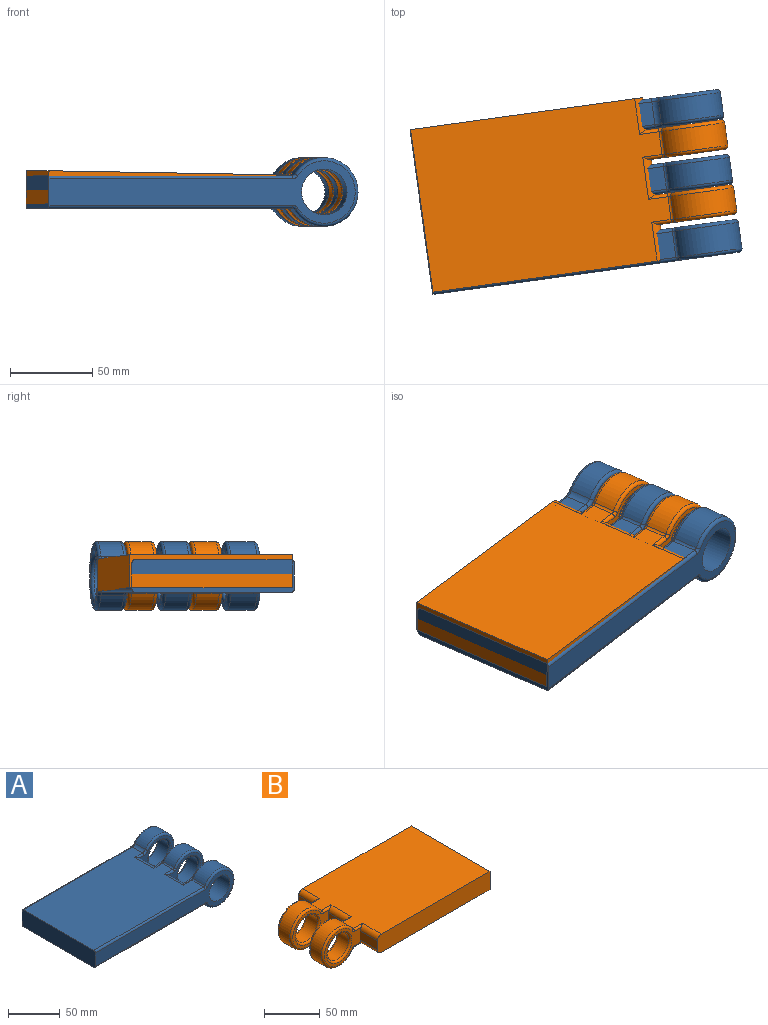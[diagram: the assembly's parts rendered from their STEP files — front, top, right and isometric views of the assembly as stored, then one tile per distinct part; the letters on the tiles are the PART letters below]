
ASSEMBLY  parts=2 mates=1
PART A: 62 faces, bbox 192.2x100x45.5 mm
  f0: plane 149.84x96mm, normal (0,0,-1), area 13745.8mm2, adj f6,f17,f19,f21,f25,f26,f27,f36
  f1: cylinder r=21mm len=42mm, axis (0,-1,0), area 1524.5mm2, adj f24,f26,f29,f34
  f2: cylinder r=21mm len=42mm, axis (0,-1,0), area 1742.3mm2, adj f23,f25,f39,f44
  f3: cylinder r=14mm len=28mm, axis (0,1,0), area 1583.4mm2, adj f8,f60
  f4: cylinder r=21mm len=42mm, axis (0,-1,0), area 1485.7mm2, adj f21,f22,f49,f54
  f5: plane 149.84x96mm, normal (0,0,1), area 13745.8mm2, adj f6,f18,f20,f22,f23,f24,f31,f32
  f6: plane 100x20mm, normal (-1,0,0), area 1996.6mm2, adj f0,f5,f7,f8,f37,f41,f47,f51
  f7: plane 188.46x38mm, normal (0,1,0), area 2751.1mm2, adj f6,f47,f48,f49,f50,f51,f61
  f8: plane 188.46x38mm, normal (0,-1,0), area 2936.7mm2, adj f3,f6,f37,f38,f39,f40,f41
  f9: cylinder r=14mm len=28mm, axis (0,1,0), area 1231.5mm2, adj f58,f61
  f10: plane 46.47x38mm, normal (0,1,0), area 462.3mm2, adj f14,f19,f20,f42,f43,f44,f45,f46
  f11: plane 46.47x38mm, normal (0,1,0), area 462.3mm2, adj f13,f17,f18,f27,f28,f29,f30,f31
  f12: cylinder r=14mm len=28mm, axis (0,1,0), area 1231.5mm2, adj f57,f59
  f13: plane 22x10mm, normal (1,0,0), area 220mm2, adj f11,f16,f17,f18
  f14: plane 22x10mm, normal (1,0,0), area 220mm2, adj f10,f15,f19,f20
  f15: plane 46.47x38mm, normal (0,-1,0), area 462.3mm2, adj f14,f19,f20,f32,f33,f34,f35,f36
  f16: plane 46.47x38mm, normal (0,-1,0), area 465.2mm2, adj f13,f17,f18,f52,f53,f54,f55,f56
  f17: cylinder r=5mm len=26mm, axis (0,1,0), area 179.9mm2, adj f0,f11,f13,f16,f27,f56
  f18: cylinder r=5mm len=26mm, axis (0,1,0), area 179.9mm2, adj f5,f11,f13,f16,f31,f52
  f19: cylinder r=5mm len=26mm, axis (0,1,0), area 179.9mm2, adj f0,f10,f14,f15,f36,f42
  f20: cylinder r=5mm len=26mm, axis (0,1,0), area 179.9mm2, adj f5,f10,f14,f15,f32,f46
  f21: cylinder r=5mm len=14mm, axis (0,-1,0), area 66.9mm2, adj f0,f4,f50,f55
  f22: cylinder r=5mm len=14mm, axis (0,-1,0), area 66.9mm2, adj f4,f5,f48,f53
  f23: cylinder r=2mm len=16mm, axis (0,-1,0), area 32.7mm2, adj f2,f5,f38,f45
  f24: cylinder r=2mm len=14mm, axis (0,-1,0), area 28.6mm2, adj f1,f5,f30,f33
  f25: cylinder r=2mm len=16mm, axis (0,-1,0), area 32.7mm2, adj f0,f2,f40,f43
  f26: cylinder r=2mm len=14mm, axis (0,-1,0), area 28.6mm2, adj f0,f1,f28,f35
  f27: cylinder r=2mm len=11.84mm, axis (-1,0,0), area 30.2mm2, adj f0,f11,f17,f28
  f28: torus R=4mm, axis (0,-1,0), area 8.8mm2, adj f11,f26,f27,f29
  f29: torus R=19mm, axis (0,-1,0), area 330.3mm2, adj f1,f11,f28,f30
  f30: torus R=4mm, axis (0,-1,0), area 8.8mm2, adj f11,f24,f29,f31
  f31: cylinder r=2mm len=11.84mm, axis (1,0,0), area 30.2mm2, adj f5,f11,f18,f30
  f32: cylinder r=2mm len=11.84mm, axis (1,0,0), area 30.2mm2, adj f5,f15,f20,f33
  f33: torus R=4mm, axis (0,1,0), area 8.8mm2, adj f15,f24,f32,f34
  f34: torus R=19mm, axis (0,1,0), area 330.3mm2, adj f1,f15,f33,f35
  f35: torus R=4mm, axis (0,1,0), area 8.8mm2, adj f15,f26,f34,f36
  f36: cylinder r=2mm len=11.84mm, axis (-1,0,0), area 30.2mm2, adj f0,f15,f19,f35
  f37: cylinder r=2mm len=149.84mm, axis (-1,0,0), area 470.7mm2, adj f5,f6,f8,f38
  f38: torus R=4mm, axis (0,-1,0), area 8.8mm2, adj f8,f23,f37,f39
  f39: torus R=19mm, axis (0,-1,0), area 330.3mm2, adj f2,f8,f38,f40
  f40: torus R=4mm, axis (0,-1,0), area 8.8mm2, adj f8,f25,f39,f41
  f41: cylinder r=2mm len=149.84mm, axis (1,0,0), area 470.7mm2, adj f0,f6,f8,f40
  f42: cylinder r=2mm len=11.84mm, axis (-1,0,0), area 30.2mm2, adj f0,f10,f19,f43
  f43: torus R=4mm, axis (0,-1,0), area 8.8mm2, adj f10,f25,f42,f44
  f44: torus R=19mm, axis (0,-1,0), area 330.3mm2, adj f2,f10,f43,f45
  f45: torus R=4mm, axis (0,-1,0), area 8.8mm2, adj f10,f23,f44,f46
  f46: cylinder r=2mm len=11.84mm, axis (1,0,0), area 30.2mm2, adj f5,f10,f20,f45
  f47: cylinder r=2mm len=148.22mm, axis (1,0,0), area 465.7mm2, adj f5,f6,f7,f48
  f48: torus R=7mm, axis (0,-1,0), area 17.2mm2, adj f7,f22,f47,f49
  f49: torus R=19mm, axis (0,-1,0), area 321.8mm2, adj f4,f7,f48,f50
  f50: torus R=7mm, axis (0,-1,0), area 17.2mm2, adj f7,f21,f49,f51
  f51: cylinder r=2mm len=148.22mm, axis (-1,0,0), area 465.7mm2, adj f0,f6,f7,f50
  f52: cylinder r=2mm len=10.23mm, axis (1,0,0), area 25.1mm2, adj f5,f16,f18,f53
  f53: torus R=7mm, axis (0,1,0), area 17.2mm2, adj f16,f22,f52,f54
  f54: torus R=19mm, axis (0,1,0), area 321.8mm2, adj f4,f16,f53,f55
  f55: torus R=7mm, axis (0,1,0), area 17.2mm2, adj f16,f21,f54,f56
  f56: cylinder r=2mm len=10.23mm, axis (-1,0,0), area 25.1mm2, adj f0,f16,f17,f55
  f57: torus R=16mm, axis (0,1,0), area 290.7mm2, adj f12,f15
  f58: torus R=16mm, axis (0,1,0), area 290.7mm2, adj f9,f16
  f59: torus R=16mm, axis (0,-1,0), area 290.7mm2, adj f11,f12
  f60: torus R=16mm, axis (0,-1,0), area 290.7mm2, adj f3,f10
  f61: torus R=16mm, axis (0,-1,0), area 290.7mm2, adj f7,f9
PART B: 50 faces, bbox 192.2x100x45.5 mm
  f0: plane 149.84x100mm, normal (0,0,-1), area 14130.9mm2, adj f6,f7,f8,f16,f18,f20,f24,f25
  f1: cylinder r=21mm len=42mm, axis (0,-1,0), area 1524.5mm2, adj f23,f25,f28,f33
  f2: cylinder r=21mm len=42mm, axis (0,-1,0), area 1524.5mm2, adj f22,f24,f38,f43
  f3: cylinder r=14mm len=28mm, axis (0,1,0), area 1231.5mm2, adj f46,f49
  f4: cylinder r=14mm len=28mm, axis (0,1,0), area 1231.5mm2, adj f47,f48
  f5: plane 149.84x100mm, normal (0,0,1), area 14130.9mm2, adj f6,f7,f8,f17,f19,f21,f22,f23
  f6: plane 142.99x20mm, normal (0,1,0), area 2849.1mm2, adj f0,f5,f8,f13,f20,f21
  f7: plane 142.99x20mm, normal (0,-1,0), area 2849.1mm2, adj f0,f5,f8,f12,f16,f17
  f8: plane 100x20mm, normal (1,0,0), area 2000mm2, adj f0,f5,f6,f7
  f9: plane 46.47x38mm, normal (0,1,0), area 462.3mm2, adj f11,f18,f19,f36,f37,f38,f39,f40
  f10: plane 46.47x38mm, normal (0,1,0), area 462.3mm2, adj f13,f20,f21,f26,f27,f28,f29,f30
  f11: plane 22x10mm, normal (-1,0,0), area 220mm2, adj f9,f14,f18,f19
  f12: plane 22x10mm, normal (-1,0,0), area 220mm2, adj f7,f15,f16,f17
  f13: plane 20x10mm, normal (-1,0,0), area 200mm2, adj f6,f10,f20,f21
  f14: plane 46.47x38mm, normal (0,-1,0), area 462.3mm2, adj f11,f18,f19,f31,f32,f33,f34,f35
  f15: plane 46.47x38mm, normal (0,-1,0), area 462.3mm2, adj f12,f16,f17,f41,f42,f43,f44,f45
  f16: cylinder r=5mm len=24mm, axis (0,1,0), area 176.3mm2, adj f0,f7,f12,f15,f45
  f17: cylinder r=5mm len=24mm, axis (0,-1,0), area 176.3mm2, adj f5,f7,f12,f15,f41
  f18: cylinder r=5mm len=26mm, axis (0,-1,0), area 179.9mm2, adj f0,f9,f11,f14,f35,f36
  f19: cylinder r=5mm len=26mm, axis (0,-1,0), area 179.9mm2, adj f5,f9,f11,f14,f31,f40
  f20: cylinder r=5mm len=22mm, axis (0,-1,0), area 160.6mm2, adj f0,f6,f10,f13,f26
  f21: cylinder r=5mm len=22mm, axis (0,1,0), area 160.6mm2, adj f5,f6,f10,f13,f30
  f22: cylinder r=2mm len=14mm, axis (0,-1,0), area 28.6mm2, adj f2,f5,f39,f42
  f23: cylinder r=2mm len=14mm, axis (0,-1,0), area 28.6mm2, adj f1,f5,f29,f32
  f24: cylinder r=2mm len=14mm, axis (0,-1,0), area 28.6mm2, adj f0,f2,f37,f44
  f25: cylinder r=2mm len=14mm, axis (0,-1,0), area 28.6mm2, adj f0,f1,f27,f34
  f26: cylinder r=2mm len=11.84mm, axis (-1,0,0), area 30.2mm2, adj f0,f10,f20,f27
  f27: torus R=4mm, axis (0,1,0), area 8.8mm2, adj f10,f25,f26,f28
  f28: torus R=19mm, axis (0,1,0), area 330.3mm2, adj f1,f10,f27,f29
  f29: torus R=4mm, axis (0,1,0), area 8.8mm2, adj f10,f23,f28,f30
  f30: cylinder r=2mm len=11.84mm, axis (1,0,0), area 30.2mm2, adj f5,f10,f21,f29
  f31: cylinder r=2mm len=11.84mm, axis (1,0,0), area 30.2mm2, adj f5,f14,f19,f32
  f32: torus R=4mm, axis (0,-1,0), area 8.8mm2, adj f14,f23,f31,f33
  f33: torus R=19mm, axis (0,-1,0), area 330.3mm2, adj f1,f14,f32,f34
  f34: torus R=4mm, axis (0,-1,0), area 8.8mm2, adj f14,f25,f33,f35
  f35: cylinder r=2mm len=11.84mm, axis (-1,0,0), area 30.2mm2, adj f0,f14,f18,f34
  f36: cylinder r=2mm len=11.84mm, axis (-1,0,0), area 30.2mm2, adj f0,f9,f18,f37
  f37: torus R=4mm, axis (0,1,0), area 8.8mm2, adj f9,f24,f36,f38
  f38: torus R=19mm, axis (0,1,0), area 330.3mm2, adj f2,f9,f37,f39
  f39: torus R=4mm, axis (0,1,0), area 8.8mm2, adj f9,f22,f38,f40
  f40: cylinder r=2mm len=11.84mm, axis (1,0,0), area 30.2mm2, adj f5,f9,f19,f39
  f41: cylinder r=2mm len=11.84mm, axis (1,0,0), area 30.2mm2, adj f5,f15,f17,f42
  f42: torus R=4mm, axis (0,-1,0), area 8.8mm2, adj f15,f22,f41,f43
  f43: torus R=19mm, axis (0,-1,0), area 330.3mm2, adj f2,f15,f42,f44
  f44: torus R=4mm, axis (0,-1,0), area 8.8mm2, adj f15,f24,f43,f45
  f45: cylinder r=2mm len=11.84mm, axis (-1,0,0), area 30.2mm2, adj f0,f15,f16,f44
  f46: torus R=16mm, axis (0,-1,0), area 290.7mm2, adj f3,f15
  f47: torus R=16mm, axis (0,-1,0), area 290.7mm2, adj f4,f14
  f48: torus R=16mm, axis (0,1,0), area 290.7mm2, adj f4,f10
  f49: torus R=16mm, axis (0,1,0), area 290.7mm2, adj f3,f9
PLACE A rot(axis=(0,0,1),7.9deg) t=(-173.43,5.79,23.12)mm fixed
PLACE B rot(axis=(0.07,-1,0),179deg) t=(-26.03,27.52,21.86)mm
MATE cylindrical B.f3 <-> A.f60  axis (0.14,-0.99,0) through (-99.5,31.5,23.12)mm
